# Revit family: ADB Gas cooktops cupboard 400
name_source: partatom
category: Equipement spécialisé
units: mm (PartAtom-declared; Revit-internal decimal feet)

## family parameters
Basée sur le plan de construction = Non
Conserver l'orientation des annotations = Non
Cote de connecteur circulaire = Utiliser le diamètre
Couper avec des vides une fois chargée = Non
Numéro OmniClass = 23.40.40.14.17.11
Partagée = Non
Repère de localisation dans la pièce = Non
Titre OmniClass = Cookers, Ovens, Stoves
Toujours verticalement = Oui
Type d'élément = Normal

## types (3) — shared parameters
C = 200 mm  [stored 0.656168 ft]
Commentaires du type = Ambassade range - Cupboards - Gas cooktops
D = 765 mm  [stored 2.50984 ft]
E = 55 mm  [stored 0.180446 ft]
Electrical Remarks = 230V(MONO) commutable 400V(TRI)
F = 810 mm
Fabricant = Société Industrielle de Lacanche
Gas Flow = 0.0 L/s
Gas Size = 20.96 mm
URL = https://www.ambassade-de-bourgogne.com
URL Cutsheet = https://www.ambassade-de-bourgogne.com
zero-valued in all types: Elévation par défaut

## per-type parameters (varying)
| type | Bouton 420 | Description | Gas power kW | Plaque | Poids base | Types 420R et 410CF |
| CMG 410 UR | Non | 5kW burner cupboard | 5 | CMG 400 - 2 - 1 feux vifs et plaque : 1 feu | 44.00 kg | Non |
| CMG 410 CF | Non | Cupboard 5kW burner - Cast iron simmer plate | 5 | CMG 400 - 2 - 1 feux vifs et plaque : Plaque coup de feu | 54.00 kg | Oui |
| CMG 420 R | Oui | 2x4kW burner cupboard | 8 | CMG 400 - 2 - 1 feux vifs et plaque : 2 feux | 43.00 kg | Oui |

note: column(s) folded — value = type name in every type: Modèle

note: [stored X ft] marks values corroborated as IEEE doubles in the binary element streams (Revit-internal decimal feet)
